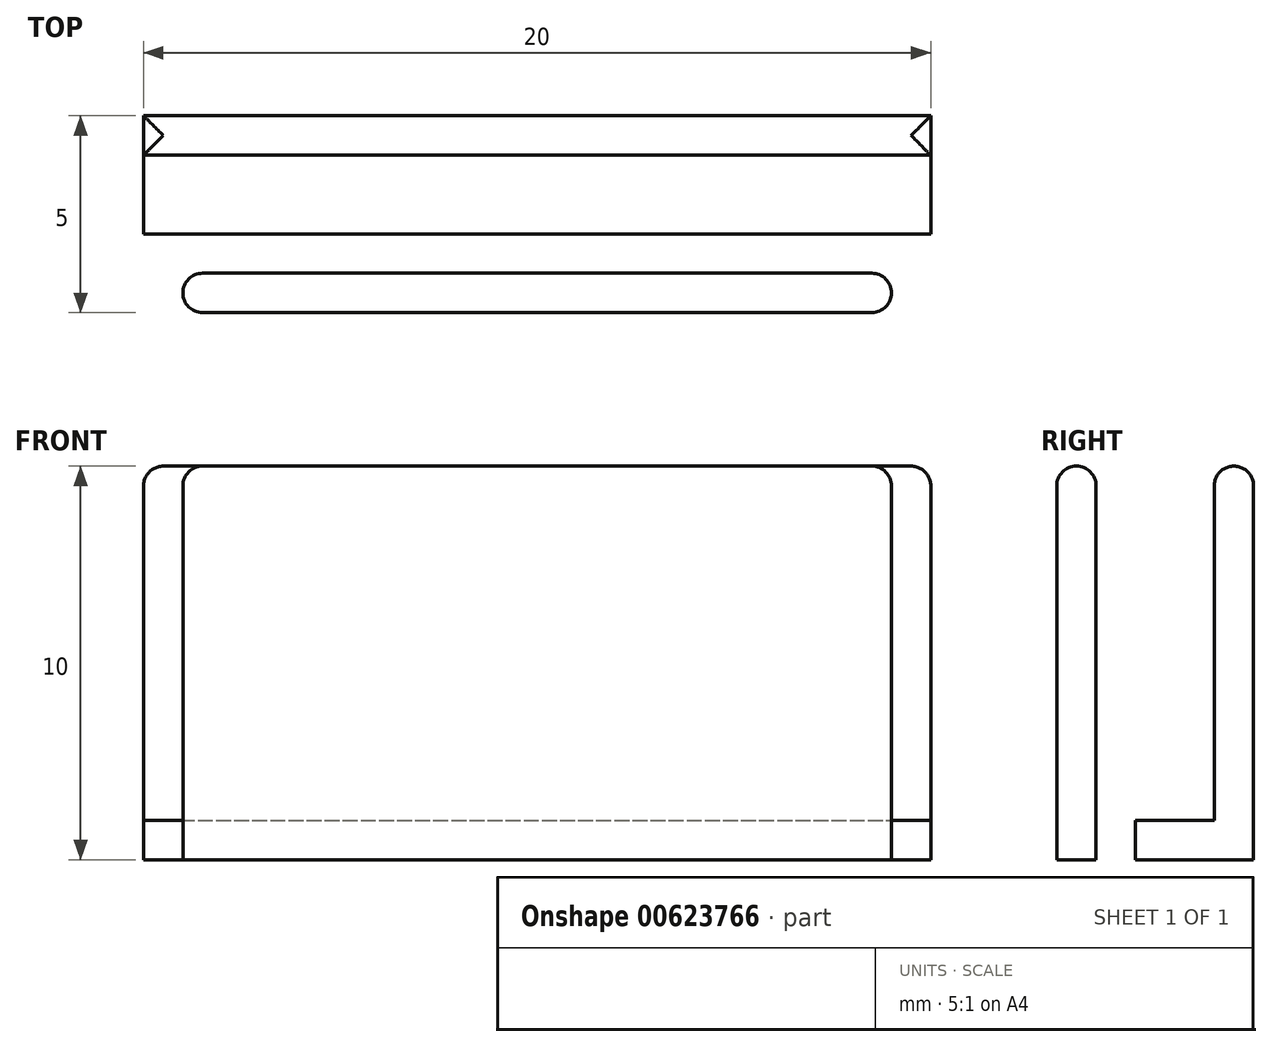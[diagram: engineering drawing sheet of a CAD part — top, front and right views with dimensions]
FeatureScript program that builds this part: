
annotation { "Feature Type Name" : "Feature", "Feature Type Description" : "" }
export const myFeature = defineFeature(function(context is Context, id is Id, definition is map)
    precondition{}
    {
        {
            var Q0;
            Q0=qCreatedBy(makeId("Top.planeOp"),FACE);
            var sketch = newSketch(context, id + "F0", { "sketchPlane" : qUnion([Q0])});
            skLineSegment(sketch, "E0.bottom", {"start": v(-10, 1) * mm, "end": v(10, 1) * mm});
            skLineSegment(sketch, "E0.top", {"start": v(-10, -1) * mm, "end": v(10, -1) * mm});
            skLineSegment(sketch, "E0.left", {"start": v(-10, 1) * mm, "end": v(-10, -1) * mm});
            skLineSegment(sketch, "E0.right", {"start": v(10, 1) * mm, "end": v(10, -1) * mm});
            skPoint(sketch, "E0.middle", {"position": v(0, 0) * mm});
            skLineSegment(sketch, "E1.bottom", {"start": v(-10, -1) * mm, "end": v(-8, -1) * mm});
            skLineSegment(sketch, "E1.top", {"start": v(-10, -2) * mm, "end": v(-8, -2) * mm});
            skLineSegment(sketch, "E1.left", {"start": v(-10, -1) * mm, "end": v(-10, -2) * mm});
            skLineSegment(sketch, "E1.right", {"start": v(-8, -1) * mm, "end": v(-8, -2) * mm});
            skLineSegment(sketch, "E2.bottom", {"start": v(10, -1) * mm, "end": v(8, -1) * mm});
            skLineSegment(sketch, "E2.top", {"start": v(10, -2) * mm, "end": v(8, -2) * mm});
            skLineSegment(sketch, "E2.left", {"start": v(10, -1) * mm, "end": v(10, -2) * mm});
            skLineSegment(sketch, "E2.right", {"start": v(8, -1) * mm, "end": v(8, -2) * mm});
            skLineSegment(sketch, "E3.bottom", {"start": v(-8, -1) * mm, "end": v(8, -1) * mm});
            skLineSegment(sketch, "E3.top", {"start": v(-8, -2) * mm, "end": v(8, -2) * mm});
            skPoint(sketch, "E4.oppositeSnap0", {"position": v(9, -2) * mm});
            skLineSegment(sketch, "E4.bottom", {"start": v(-9, -2) * mm, "end": v(9, -2) * mm});
            skLineSegment(sketch, "E4.top", {"start": v(-9, -3) * mm, "end": v(9, -3) * mm});
            skLineSegment(sketch, "E4.left", {"start": v(-9, -2) * mm, "end": v(-9, -3) * mm});
            skLineSegment(sketch, "E4.right", {"start": v(9, -2) * mm, "end": v(9, -3) * mm});
            skLineSegment(sketch, "E5.top", {"start": v(-10, 2) * mm, "end": v(10, 2) * mm});
            skLineSegment(sketch, "E5.left", {"start": v(-10, 1) * mm, "end": v(-10, 2) * mm});
            skLineSegment(sketch, "E5.right", {"start": v(10, 1) * mm, "end": v(10, 2) * mm});
            skSolve(sketch);
        }
        {
            var Q0;
            Q0=makeQuery(id+"F0.imprint","IMPRINT",FACE,{"disambiguationData":[TD([[makeQuery(id+"F0.imprint","IMPRINT",EDGE,{"derivedFrom":sQuery(id+"F0.wireOp",EDGE,"E0.left")}),1.0]])]});
            var Q1;
            Q1=makeQuery(id+"F0.imprint","IMPRINT",FACE,{"disambiguationData":[TD([[makeQuery(id+"F0.imprint","IMPRINT",EDGE,{"derivedFrom":sQuery(id+"F0.wireOp",EDGE,"E3.bottom")}),-1.0]])]});
            extrude(context, id + "F1", {"entities" : qUnion([Q0, Q1]), "depth" : 1 * mm, "offsetDistance" : 25 * mm});
        }
        {
            var Q0;
            Q0=makeQuery(id+"F0.imprint","IMPRINT",FACE,{"disambiguationData":[TD([[makeQuery(id+"F0.imprint","IMPRINT",EDGE,{"derivedFrom":sQuery(id+"F0.wireOp",EDGE,"E0.bottom")}),1.0]])]});
            var Q1;
            Q1=makeQuery(id+"F0.imprint","IMPRINT",FACE,{"disambiguationData":[TD([[makeQuery(id+"F0.imprint","IMPRINT",EDGE,{"derivedFrom":sQuery(id+"F0.wireOp",EDGE,"E1.bottom")}),-1.0]])]});
            var Q2;
            Q2=makeQuery(id+"F0.imprint","IMPRINT",FACE,{"disambiguationData":[TD([[makeQuery(id+"F0.imprint","IMPRINT",EDGE,{"derivedFrom":sQuery(id+"F0.wireOp",EDGE,"E4.top")}),1.0]])]});
            var Q3;
            Q3=makeQuery(id+"F0.imprint","IMPRINT",FACE,{"disambiguationData":[TD([[makeQuery(id+"F0.imprint","IMPRINT",EDGE,{"derivedFrom":sQuery(id+"F0.wireOp",EDGE,"E2.bottom")}),1.0]])]});
            extrude(context, id + "F2", {"entities" : qUnion([Q0, Q1, Q2, Q3]), "operationType" : NewBodyOperationType.ADD, "depth" : 10 * mm, "offsetDistance" : 25 * mm});
        }
        {
            var Q0;
            Q0=makeQuery(id+"F2.opExtrude","SWEPT_EDGE",EDGE,{"disambiguationData":[OSD([sQuery(id+"F0.wireOp",EDGE,"E1.top"),sQuery(id+"F0.wireOp",EDGE,"E4.bottom"),sQuery(id+"F0.wireOp",EDGE,"E4.left")])]});
            var Q1;
            Q1=makeQuery(id+"F2.opExtrude","SWEPT_EDGE",EDGE,{"disambiguationData":[OSD([sQuery(id+"F0.wireOp",EDGE,"E4.top"),sQuery(id+"F0.wireOp",EDGE,"E4.left")])]});
            var Q2;
            Q2=makeQuery(id+"F2.opExtrude","SWEPT_EDGE",EDGE,{"disambiguationData":[OSD([sQuery(id+"F0.wireOp",EDGE,"E2.top"),sQuery(id+"F0.wireOp",EDGE,"E4.bottom"),sQuery(id+"F0.wireOp",EDGE,"E4.right")])]});
            var Q3;
            Q3=makeQuery(id+"F2.opExtrude","SWEPT_EDGE",EDGE,{"disambiguationData":[OSD([sQuery(id+"F0.wireOp",EDGE,"E4.top"),sQuery(id+"F0.wireOp",EDGE,"E4.right")])]});
            var Q4;
            Q4=makeQuery(id+"F2.opExtrude","CAP_FACE",FACE,{"disambiguationData":[OSD([sQuery(id+"F0.wireOp",EDGE,"E1.bottom"),sQuery(id+"F0.wireOp",EDGE,"E1.top"),sQuery(id+"F0.wireOp",EDGE,"E1.left"),sQuery(id+"F0.wireOp",EDGE,"E2.bottom"),sQuery(id+"F0.wireOp",EDGE,"E2.top"),sQuery(id+"F0.wireOp",EDGE,"E2.left"),sQuery(id+"F0.wireOp",EDGE,"E1.right"),sQuery(id+"F0.wireOp",EDGE,"E2.right"),sQuery(id+"F0.wireOp",EDGE,"E4.bottom"),sQuery(id+"F0.wireOp",EDGE,"E4.top"),sQuery(id+"F0.wireOp",EDGE,"E4.left"),sQuery(id+"F0.wireOp",EDGE,"E4.right")])],"isStart":false});
            var Q5;
            Q5=makeQuery(id+"F2.opExtrude","CAP_FACE",FACE,{"disambiguationData":[OSD([sQuery(id+"F0.wireOp",EDGE,"E0.bottom"),sQuery(id+"F0.wireOp",EDGE,"E5.top"),sQuery(id+"F0.wireOp",EDGE,"E5.left"),sQuery(id+"F0.wireOp",EDGE,"E5.right")])],"isStart":false});
            fillet(context, id + "F3", {"entities" : qUnion([Q0, Q1, Q2, Q3, Q4, Q5]), "radius" : .5 * mm, "tangentPropagation" : true, "allowEdgeOverflow" : false});
        }
    });
